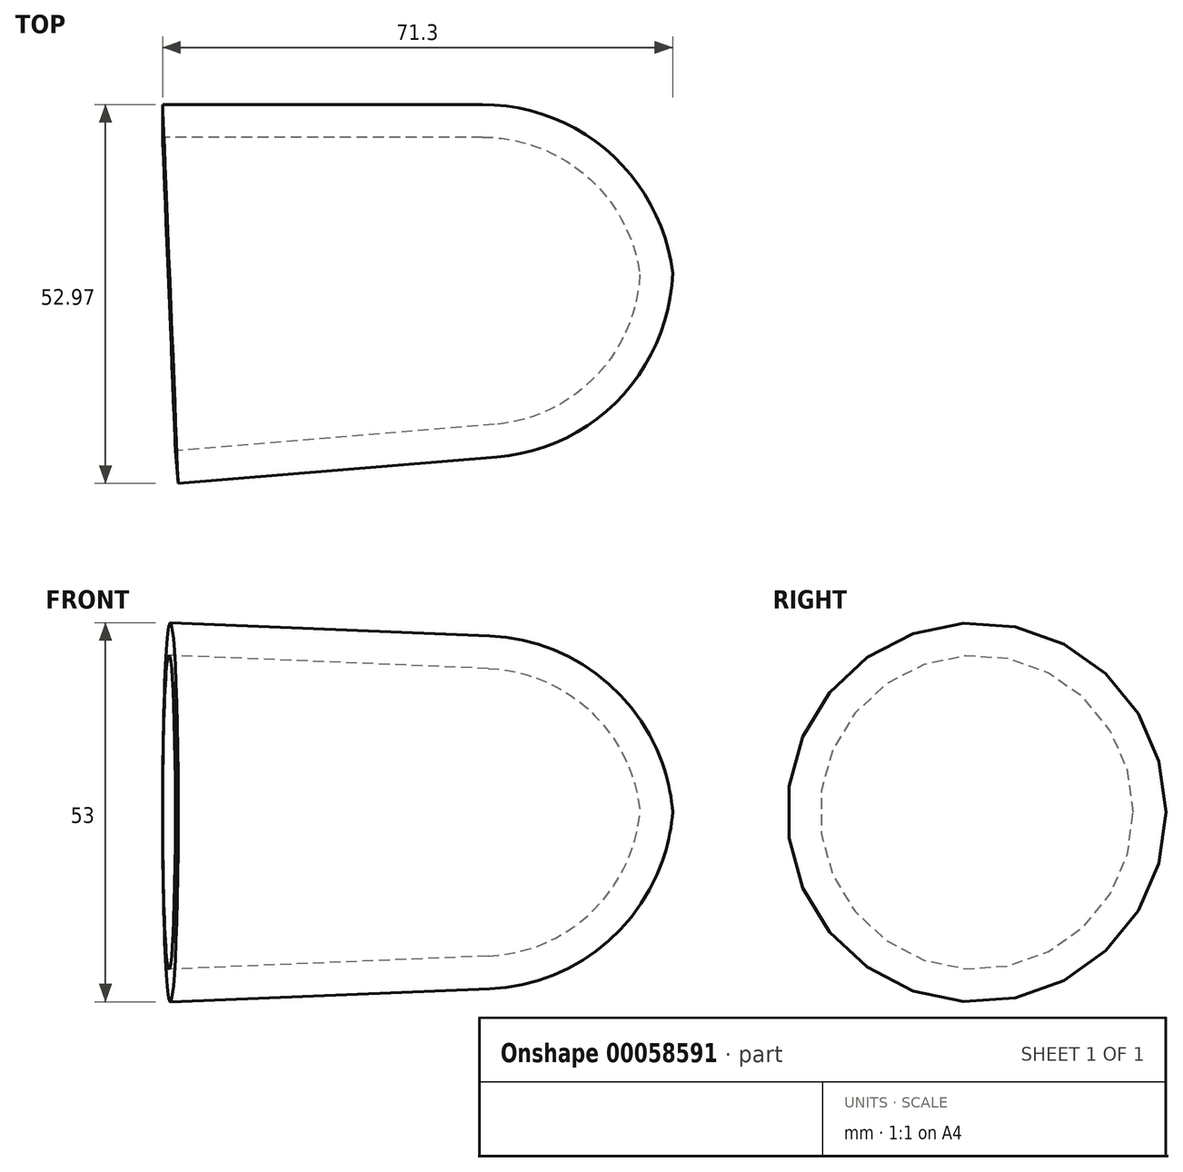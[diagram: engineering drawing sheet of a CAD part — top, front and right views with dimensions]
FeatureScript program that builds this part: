
annotation { "Feature Type Name" : "Feature", "Feature Type Description" : "" }
export const myFeature = defineFeature(function(context is Context, id is Id, definition is map)
    precondition{}
    {
        {
            var Q0;
            Q0=qCreatedBy(makeId("Top.planeOp"),FACE);
            var sketch = newSketch(context, id + "F0", { "sketchPlane" : qUnion([Q0])});
            skArc(sketch, "E0", {"start": v(0, 26.78) * mm, "mid": v(17.78, 20.03) * mm, "end": v(26.6, 3.18) * mm});
            skArc(sketch, "E1.0", {"start": v(0, 22.2) * mm, "mid": v(14.6, 16.73) * mm, "end": v(22, 2.99) * mm});
            skLineSegment(sketch, "E2", {"start": v(-0.46, 22.23) * mm, "end": v(0, 22.2) * mm});
            skLineSegment(sketch, "E3.0", {"start": v(26.6, 3.17) * mm, "end": v(22, 2.99) * mm});
            skPoint(sketch, "E4.start.orphan", {"position": v(26.78, 0) * mm});
            skLineSegment(sketch, "E5", {"start": v(0, 22.2) * mm, "end": v(-44.71, 22.2) * mm});
            skLineSegment(sketch, "E6", {"start": v(0, 26.78) * mm, "end": v(-44.71, 26.78) * mm});
            skLineSegment(sketch, "E7", {"start": v(-44.71, 22.2) * mm, "end": v(-44.71, 26.78) * mm});
            skSolve(sketch);
        }
        {
            var Q0;
            Q0 = qSketchRegion(id + "F0", true);
            var Q1;
            Q1=sQuery(id+"F0.wireOp",EDGE,"E3.0");
            revolve(context, id + "F1", {"entities" : qUnion([Q0]), "axis" : qUnion([Q1]), "revolveType" : RevolveType.ONE_DIRECTION, "angle" : 360 * degree});
        }
    });
